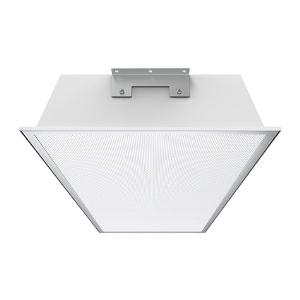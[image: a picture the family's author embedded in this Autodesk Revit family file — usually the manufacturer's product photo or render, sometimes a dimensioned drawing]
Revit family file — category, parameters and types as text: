
# Revit family: 3f_filippi_-_beta_500_sp_3f_filippi_-_52002_-_beta_500_200w-840_sp_l870
name_source: partatom
category: Lighting Fixtures
units: mm (PartAtom-declared; Revit-internal decimal feet)

## family parameters
Cut with Voids When Loaded = No
Host = Face
Light Source = No
Part Type = Normal
Room Calculation Point = No
Round Connector Dimension = Use Diameter
Shared = No

## types (1)
- 3F Filippi - Beta 500 SP (1 x LED, 30534 lm, 198 W, 4000 K)
    Apparent Load = 198 VA
    Approval mark = CE
    CIE Flux Codes = 62 89 97 100 100
    Color Rendering = 80
    Color Temperature = 4000 K
    Control Gear = Electronic ballast
    Default Elevation = 1800 mm
    Description = ILLUMINOTECHNICAL
Luminous efficiency 100% (DLOR 100%, ULOR 0%).
Initial luminous flux of the luminaire 30534 lm.
Direct symmetric medium distribution.
Installation Interdistance Transv.D = 1.23 x hu - Long.D = 1.25 x hu.
Tabular UGR (CIE 117 - 4H-8H; S=0.25H; 70/50/20): RUG 24.3 - 24.4.
Beam angle: 87° - 91°.
Luminous efficacy 154 lm/W.
Lifetime (L93/B10): 30000 h. (tq+25°C)
Lifetime (L90/B10): 50000 h. (tq+25°C)
Lifetime (L85/B10): 80000 h. (tq+25°C)
Lifetime (L80/B10): 100000 h. (tq+25°C)
Lifetime (L85/B10): 50000 h. (tq+45°C)
Sudden decreased luminous flux after 50000 hours: 0% (C0).
Photobiological safety in compliance with IEC/TR 62778: RG0 risk exempt, (IEC 62471).
In compliance with IEC/EN 62722-2-1 - IEC/EN 62717 standards.

SOURCE
4 linear LED modules 50W/840.
Energy efficiency class (UE 2019/2020 - UE 2019/2015): C.
CIE 13.3 Colour rendering index: CRI >80 (R9 <50%).
IES TM-30 Fidelity Index: Rf = 84 Rg = 95.
CCT nominal colour temperature 4000 K.
Colour initial tolerance (MacAdam): SDCM 3.

MECHANICAL
Housing in white painted epoxy-polyester powder aluminium.
White aluminium non-iridescent high efficiency.
SP transparent methacrylate (PMMA) diffuser, prismatic outside, antiglare.
Perimetrical frame in stainless steel with vandal-proof opening and stainless steel nuts and bolts.
Polyurethane foam seal, ecological, anti-aging, installed using a continuous automatic process with no joints.
Fixing bracket in stainless steel.
Luminaire with limited surface temperature. - D - (EN 60598-2-24)
Dimensions: 870x515 mm, height 105 mm. Weight 9.485 kg.
IP66 protection degree.
Mechanical strength to impacts IK07 (2 joule).
Glow-wire test resistance 850°C.

ELECTRICAL
Halogen Free electronic wiring 230V-50/60Hz, power factor 0.95, THD <25%, constant output current, class I, 2 driver.
Twin-circuit.
Power of the luminaire 198 W.
ENEC - CE.
SAFE FLICKER: PstLM=<1 and SVM=<0.4 (IEC TR 61547-1 and IEC TR 63158), to ensure a more comfortable and safe light.
Luminaire compliant with EN 60598-2-22 for power supply from a centralised emergency system CPSS (Central Power Supply System), not incorporated in the luminaire - high risk areas excluded. The default power and flux are 100% in AC and 100% in DC.
Ambient temperature from -20°C to +45°C.
Temperature class T6 max 85°C.
Quick connection via M20 3P connector with 9-13 mm tightening range.
Quick connection in polycarbonate with M20x1,5 cable gland, to access the terminal block positioned on a removable runner.
Relative humidity UR: <85%.

INSTALLATION
Ceiling / Suspended.
All accessories dedicated to this product are available on the Catalog and on our website www.3F-Filippi.com.

APPLICATIONS
Suitable product for food production plants (HACCP), IFS (Food Version 6), BRC (GSFS Food Version 7).
Commercial and industrial environments and warehouses.

WARNING
Fixture not suitable for cold stores with an ambient temperature <0°C and/or relative humidity >85%.
Luminaire designed for disposal/recycling at end-of-life.
Replaceable (LED only) light source by a professional. Replaceable control gear by a professional.
    Height = 105 mm
    Lamp = 1 x LED
    Lamp Light Flux = 30534 lm
    Lamp Power = 198 W
    Lamp count = 1
    Length = 870 mm
    Lifetime = 50000 h
    Luminous efficacy = 154 lm/W
    Manufacturer = 3F Filippi
    ModVariant = No
    Model = 3F Filippi - 52002 - Beta 500 200W-840 SP L870
    Mounting Place = Ceiling
    Mounting Type = Pendant
    Number of Poles = 1
    OnlyDefault = Yes
    Power Factor = 1
    Product Name = 3F Filippi - Beta 500 SP
    Product group = pendant luminaire
    ProductGroupID = 9
    Protection Class = Protection class I
    Protection Degree = IP 66
    RLX_Detail_Level = 1
    RLX_Emergency_Light_Flux = 0 lm
    RLX_Emergency_Type = 0
    RLX_Emergency_Type_DB = No
    RlxData = <blob elided: 132589 chars, md5=b37910b5>
    Socket = socket
    Standby Power = 0 W
    System Light Flux = 30534 lm
    System Power = 198 W
    Type Comments = Product without accessories
    Type Image = 3ffilippi_beta_500_sp_pc.jpg
    URL = http://relux.com
    VarID = ---
    Voltage = 0 V
    Weight = 0.00 kg
    Width = 515 mm

## geometry (parser evidence)
native form markers: Blend x4, Sweep x11
no freeform markers — native parametric forms only
